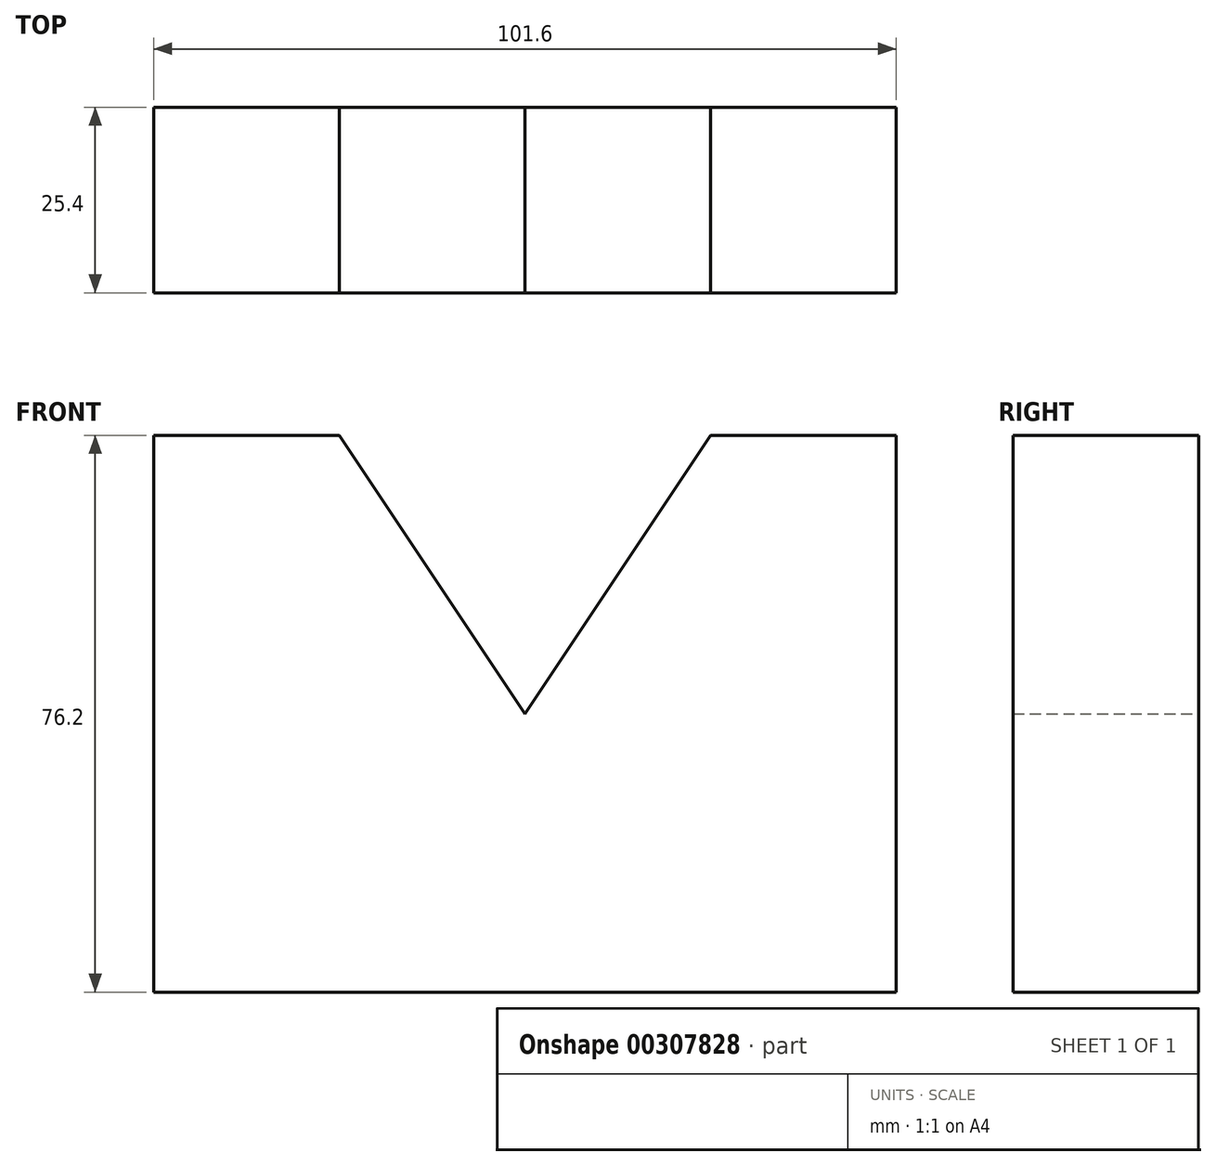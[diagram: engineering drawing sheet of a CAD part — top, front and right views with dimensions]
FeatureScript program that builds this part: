
annotation { "Feature Type Name" : "Feature", "Feature Type Description" : "" }
export const myFeature = defineFeature(function(context is Context, id is Id, definition is map)
    precondition{}
    {
        {
            var Q0;
            Q0=qCreatedBy(makeId("Front.planeOp"),FACE);
            var sketch = newSketch(context, id + "F0", { "sketchPlane" : qUnion([Q0])});
            skLineSegment(sketch, "E0", {"start": v(-58.48, -54.55) * mm, "end": v(43.12, -54.55) * mm});
            skLineSegment(sketch, "E1", {"start": v(43.12, -54.55) * mm, "end": v(43.12, 21.65) * mm});
            skLineSegment(sketch, "E2", {"start": v(-58.48, 21.65) * mm, "end": v(-58.48, -54.55) * mm});
            skLineSegment(sketch, "E3", {"start": v(43.12, 21.65) * mm, "end": v(17.72, 21.65) * mm});
            skLineSegment(sketch, "E4", {"start": v(-58.48, 21.65) * mm, "end": v(-33.08, 21.65) * mm});
            skLineSegment(sketch, "E5", {"start": v(-33.08, 21.65) * mm, "end": v(-7.68, -16.45) * mm});
            skLineSegment(sketch, "E6", {"start": v(17.72, 21.65) * mm, "end": v(-7.68, -16.45) * mm});
            skSolve(sketch);
        }
        {
            var Q0;
            Q0=makeQuery(id+"F0.imprint","IMPRINT",FACE,{"disambiguationData":[TD([[makeQuery(id+"F0.imprint","IMPRINT",EDGE,{"derivedFrom":sQuery(id+"F0.wireOp",EDGE,"E0")}),1.0]])]});
            extrude(context, id + "F1", {"entities" : qUnion([Q0]), "depth" : 25.4 * mm});
        }
    });
